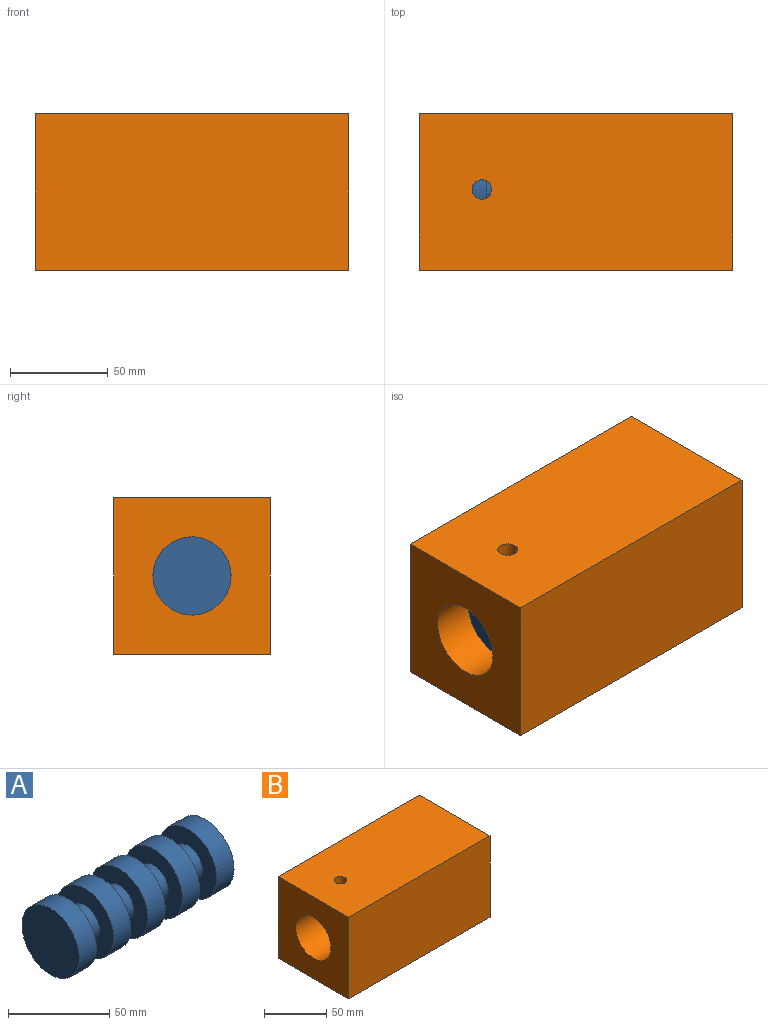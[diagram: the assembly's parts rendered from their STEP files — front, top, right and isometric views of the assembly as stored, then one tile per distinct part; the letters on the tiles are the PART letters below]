
ASSEMBLY  parts=2 mates=1
PART A: 19 faces, bbox 108x40x40 mm
  f0: plane 40x40mm, normal (-1,0,0), area 1256.6mm2, adj f18
  f1: plane 40x40mm, normal (1,0,0), area 1256.6mm2, adj f2
  f2: cylinder r=20mm len=40mm, axis (-1,0,0), area 1508mm2, adj f1,f3
  f3: plane 40x40mm, normal (-1,0,0), area 942.5mm2, adj f2,f4
  f4: cylinder r=10mm len=20mm, axis (-1,0,0), area 754mm2, adj f3,f5
  f5: plane 40x40mm, normal (1,0,0), area 942.5mm2, adj f4,f6
  f6: cylinder r=20mm len=40mm, axis (-1,0,0), area 1508mm2, adj f5,f7
  f7: plane 40x40mm, normal (-1,0,0), area 942.5mm2, adj f6,f8
  f8: cylinder r=10mm len=20mm, axis (-1,0,0), area 754mm2, adj f7,f9
  f9: plane 40x40mm, normal (1,0,0), area 942.5mm2, adj f8,f10
  f10: cylinder r=20mm len=40mm, axis (-1,0,0), area 1508mm2, adj f9,f11
  f11: plane 40x40mm, normal (-1,0,0), area 942.5mm2, adj f10,f12
  f12: cylinder r=10mm len=20mm, axis (-1,0,0), area 754mm2, adj f11,f13
  f13: plane 40x40mm, normal (1,0,0), area 942.5mm2, adj f12,f14
  f14: cylinder r=20mm len=40mm, axis (-1,0,0), area 1508mm2, adj f13,f15
  f15: plane 40x40mm, normal (-1,0,0), area 942.5mm2, adj f14,f16
  f16: cylinder r=10mm len=20mm, axis (-1,0,0), area 754mm2, adj f15,f17
  f17: plane 40x40mm, normal (1,0,0), area 942.5mm2, adj f16,f18
  f18: cylinder r=20mm len=40mm, axis (-1,0,0), area 1508mm2, adj f0,f17
PART B: 8 faces, bbox 160x80x80 mm
  f0: plane 160x80mm, normal (0,-1,0), area 12800mm2, adj f1,f3,f5,f6
  f1: plane 160x80mm, normal (0,0,-1), area 12800mm2, adj f0,f2,f5,f6
  f2: plane 160x80mm, normal (0,1,0), area 12800mm2, adj f1,f3,f5,f6
  f3: plane 160x80mm, normal (0,0,1), area 12721.5mm2, adj f0,f2,f5,f6,f7
  f4: cylinder r=20mm len=160mm, axis (-1,0,0), area 20026.7mm2, adj f5,f6,f7
  f5: plane 80x80mm, normal (1,0,0), area 5143.4mm2, adj f0,f1,f2,f3,f4
  f6: plane 80x80mm, normal (-1,0,0), area 5143.4mm2, adj f0,f1,f2,f3,f4
  f7: cylinder r=5mm len=20.99mm, axis (0,0,1), area 639.5mm2, adj f3,f4
PLACE A rot(axis=(-1,0,0),3.6deg) t=(-3.73,-11.04,2.63)mm
PLACE B t=(0,-11.04,2.63)mm fixed
MATE cylindrical B.f4 <-> A.f2  axis (-1,0,0) through (0,-11.04,2.63)mm
